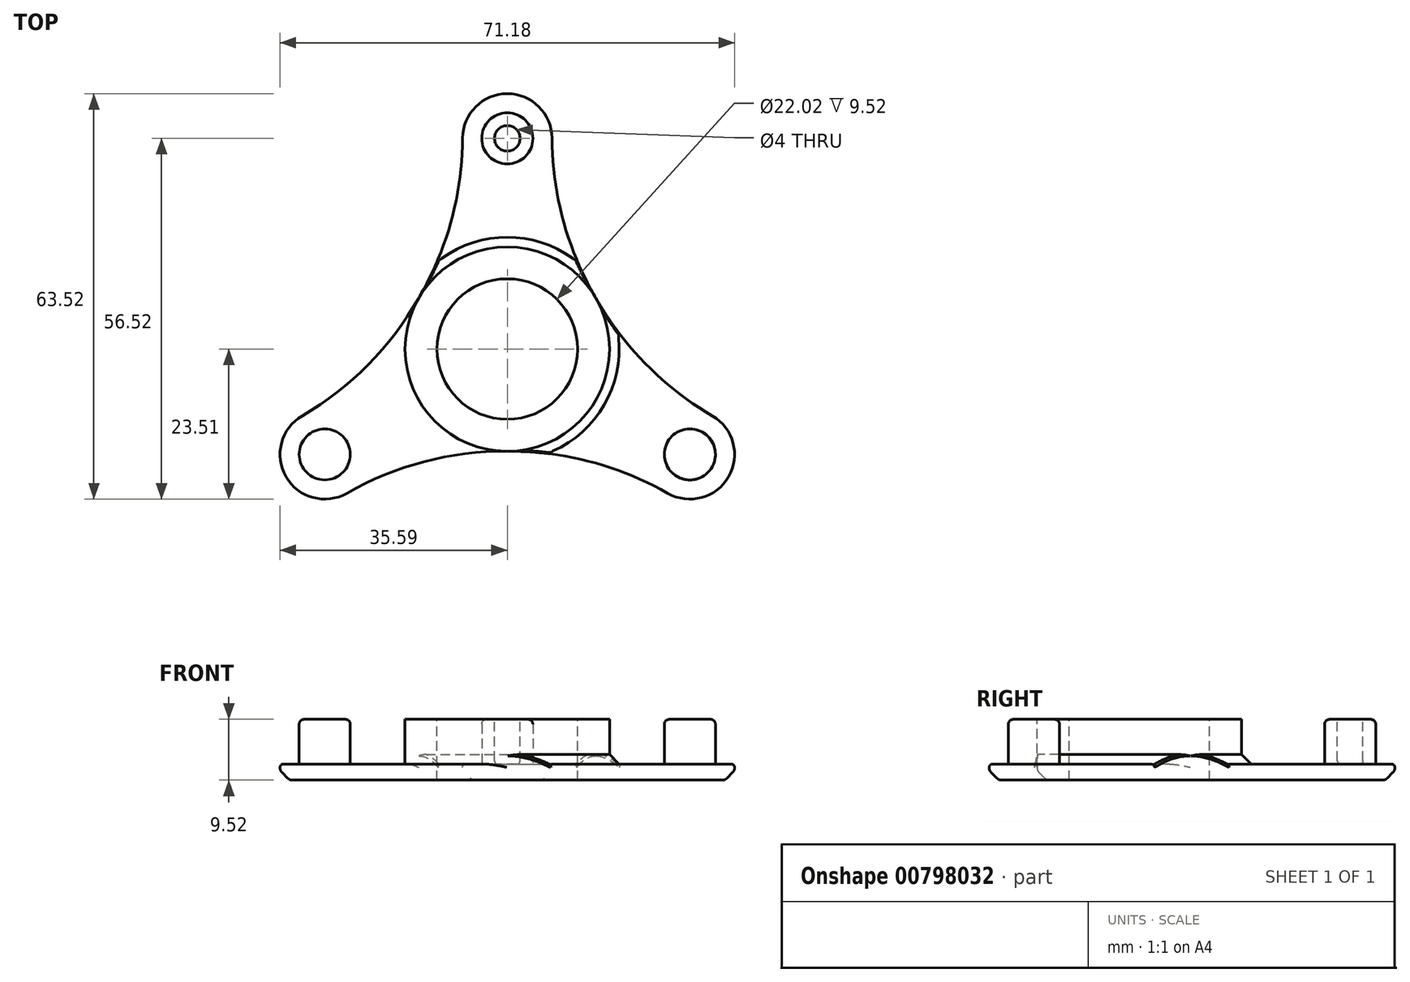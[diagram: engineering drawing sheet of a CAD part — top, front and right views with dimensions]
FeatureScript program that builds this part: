
annotation { "Feature Type Name" : "Feature", "Feature Type Description" : "" }
export const myFeature = defineFeature(function(context is Context, id is Id, definition is map)
    precondition{}
    {
        {
            var Q0;
            Q0=qCreatedBy(makeId("Top.planeOp"),FACE);
            var sketch = newSketch(context, id + "F0", { "sketchPlane" : qUnion([Q0])});
            skCircle(sketch, "E0", {"center": v(0, 0) * mm, "radius": 11.01 * mm});
            skCircle(sketch, "E1", {"center": v(0, 33.01) * mm, "radius": 4 * mm});
            skCircle(sketch, "E2.0", {"center": v(0, 33.01) * mm, "radius": 12 * mm});
            skCircle(sketch, "E3.0", {"center": v(0, 0) * mm, "radius": 16 * mm});
            skSolve(sketch);
        }
        {
            var Q0;
            Q0=makeQuery(id+"F0.imprint","IMPRINT",FACE,{"disambiguationData":[TD([[makeQuery(id+"F0.imprint","IMPRINT",EDGE,{"derivedFrom":sQuery(id+"F0.wireOp",EDGE,"E0")}),-1.0]])]});
            var Q1;
            Q1=makeQuery(id+"F0.imprint","IMPRINT",FACE,{"disambiguationData":[TD([[makeQuery(id+"F0.imprint","IMPRINT",EDGE,{"derivedFrom":sQuery(id+"F0.wireOp",EDGE,"E1")}),1.0]])]});
            extrude(context, id + "F1", {"entities" : qUnion([Q0, Q1]), "depth" : 7.02 * mm, "offsetDistance" : 25 * mm});
        }
        {
            var Q0;
            Q0=makeQuery(id+"F1.opExtrude","CAP_FACE",FACE,{"disambiguationData":[OSD([sQuery(id+"F0.wireOp",EDGE,"E0"),sQuery(id+"F0.wireOp",EDGE,"E3.0")])],"isStart":true});
            var sketch = newSketch(context, id + "F2", { "sketchPlane" : qUnion([Q0])});
            skCircle(sketch, "E4", {"center": v(-57, -33.3) * mm, "radius": 50 * mm});
            skCircle(sketch, "E5", {"center": v(57, -33.3) * mm, "radius": 50 * mm});
            skCircle(sketch, "E6", {"center": v(0, -33.01) * mm, "radius": 7 * mm});
            skSolve(sketch);
        }
        {
            var Q0;
            {var subQ0=sQuery(id+"F2.wireOp",EDGE,"E6");var subQ1=makeQuery(id+"F2.imprint","INTERSECT",VERTEX,{"derivedFrom":[sQuery(id+"F2.wireOp",EDGE,"E4"),subQ0]});Q0=makeQuery(id+"F2.imprint","IMPRINT",FACE,{"disambiguationData":[TD([[makeQuery(id+"F2.imprint","IMPRINT",EDGE,{"disambiguationData":[TD([[subQ1,1.0]])],"derivedFrom":subQ0}),1.0]])]});}
            var Q1;
            {var subQ0=sQuery(id+"F2.wireOp",EDGE,"E6");var subQ1=sQuery(id+"F2.wireOp",EDGE,"E4");var subQ2=makeQuery(id+"F2.imprint","INTERSECT",VERTEX,{"derivedFrom":[subQ1,subQ0]});Q1=makeQuery(id+"F2.imprint","IMPRINT",FACE,{"disambiguationData":[TD([[makeQuery(id+"F2.imprint","IMPRINT",EDGE,{"disambiguationData":[TD([[subQ2,-1.0]])],"derivedFrom":subQ1}),-1.0]])]});}
            var Q2;
            Q2=makeQuery(id+"F0.imprint","IMPRINT",FACE,{"disambiguationData":[TD([[makeQuery(id+"F0.imprint","IMPRINT",EDGE,{"derivedFrom":sQuery(id+"F0.wireOp",EDGE,"E0")}),-1.0]])]});
            extrude(context, id + "F3", {"entities" : qUnion([Q0, Q1, Q2]), "depth" : 2.5 * mm, "offsetDistance" : 25 * mm});
        }
        {
            var Q0;
            Q0=makeQuery(id+"F3.opExtrude","SWEPT_BODY",BODY,{"disambiguationData":[OSD([sQuery(id+"F0.wireOp",EDGE,"E3.0"),sQuery(id+"F2.wireOp",EDGE,"E4"),sQuery(id+"F2.wireOp",EDGE,"E5"),sQuery(id+"F2.wireOp",EDGE,"E6")])]});
            var Q1;
            Q1=makeQuery(id+"F1.opExtrude","SWEPT_BODY",BODY,{"disambiguationData":[OSD([sQuery(id+"F0.wireOp",EDGE,"E1")])]});
            var Q2;
            Q2=makeQuery(id+"F1.opExtrude","CAP_EDGE",EDGE,{"disambiguationData":[OSD([sQuery(id+"F0.wireOp",EDGE,"E0")])],"isStart":false});
            circularPattern(context, id + "F4", {"entities" : qUnion([Q0, Q1]), "axis" : qUnion([Q2]), "angle" : 360 * degree, "instanceCount" : 3, "equalSpace" : true});
        }
        {
            var Q0;
            Q0=makeQuery(id+"F4.opPattern","COPY",BODY,{"derivedFrom":makeQuery(id+"F3.opExtrude","SWEPT_BODY",BODY,{"disambiguationData":[OSD([sQuery(id+"F0.wireOp",EDGE,"E3.0"),sQuery(id+"F2.wireOp",EDGE,"E4"),sQuery(id+"F2.wireOp",EDGE,"E5"),sQuery(id+"F2.wireOp",EDGE,"E6")])]}),"instanceName":"2"});
            var Q1;
            Q1=makeQuery(id+"F4.opPattern","COPY",BODY,{"derivedFrom":makeQuery(id+"F1.opExtrude","SWEPT_BODY",BODY,{"disambiguationData":[OSD([sQuery(id+"F0.wireOp",EDGE,"E1")])]}),"instanceName":"2"});
            var Q2;
            Q2=makeQuery(id+"F4.opPattern","COPY",BODY,{"derivedFrom":makeQuery(id+"F3.opExtrude","SWEPT_BODY",BODY,{"disambiguationData":[OSD([sQuery(id+"F0.wireOp",EDGE,"E3.0"),sQuery(id+"F2.wireOp",EDGE,"E4"),sQuery(id+"F2.wireOp",EDGE,"E5"),sQuery(id+"F2.wireOp",EDGE,"E6")])]}),"instanceName":"1"});
            var Q3;
            Q3=makeQuery(id+"F3.opExtrude","SWEPT_BODY",BODY,{"disambiguationData":[OSD([sQuery(id+"F0.wireOp",EDGE,"E3.0"),sQuery(id+"F2.wireOp",EDGE,"E4"),sQuery(id+"F2.wireOp",EDGE,"E5"),sQuery(id+"F2.wireOp",EDGE,"E6")])]});
            var Q4;
            Q4=makeQuery(id+"F4.opPattern","COPY",BODY,{"derivedFrom":makeQuery(id+"F1.opExtrude","SWEPT_BODY",BODY,{"disambiguationData":[OSD([sQuery(id+"F0.wireOp",EDGE,"E1")])]}),"instanceName":"1"});
            var Q5;
            Q5=makeQuery(id+"F3.opExtrude","SWEPT_BODY",BODY,{"disambiguationData":[OSD([sQuery(id+"F0.wireOp",EDGE,"E0"),sQuery(id+"F0.wireOp",EDGE,"E3.0")])]});
            var Q6;
            Q6=makeQuery(id+"F1.opExtrude","SWEPT_BODY",BODY,{"disambiguationData":[OSD([sQuery(id+"F0.wireOp",EDGE,"E1")])]});
            var Q7;
            Q7=makeQuery(id+"F1.opExtrude","SWEPT_BODY",BODY,{"disambiguationData":[OSD([sQuery(id+"F0.wireOp",EDGE,"E0"),sQuery(id+"F0.wireOp",EDGE,"E3.0")])]});
            booleanBodies(context, id + "F5", {"operationType" : BooleanOperationType.UNION, "tools" : qUnion([Q0, Q1, Q2, Q3, Q4, Q5, Q6, Q7])});
        }
        {
            var Q0;
            Q0=makeQuery(id+"F4.opPattern","COPY",EDGE,{"derivedFrom":makeQuery(id+"F3.opExtrude","CAP_EDGE",EDGE,{"disambiguationData":[OSD([sQuery(id+"F2.wireOp",EDGE,"E4")])],"isStart":false}),"instanceName":"2"});
            var Q1;
            {var subQ0=sQuery(id+"F0.wireOp",EDGE,"E3.0");var subQ1=makeQuery(id+"F1.opExtrude","CAP_EDGE",EDGE,{"disambiguationData":[OSD([subQ0])],"isStart":true});Q1=makeQuery(id+"F4.opPattern","COPY",EDGE,{"derivedFrom":makeQuery(id+"F3.opExtrude","CAP_EDGE",EDGE,{"disambiguationData":[OSD([subQ0]),TDD([makeQuery(id+"F2.imprint","IMPRINT",EDGE,{"disambiguationData":[TD([[makeQuery(id+"F2.imprint","INTERSECT",VERTEX,{"derivedFrom":[subQ1,sQuery(id+"F2.wireOp",EDGE,"E4")]}),1.0]])],"derivedFrom":subQ1})])],"isStart":true}),"instanceName":"2"});}
            var Q2;
            {var subQ0=sQuery(id+"F0.wireOp",EDGE,"E3.0");var subQ1=makeQuery(id+"F1.opExtrude","CAP_EDGE",EDGE,{"disambiguationData":[OSD([subQ0])],"isStart":true});Q2=makeQuery(id+"F4.opPattern","COPY",EDGE,{"derivedFrom":makeQuery(id+"F3.opExtrude","CAP_EDGE",EDGE,{"disambiguationData":[OSD([subQ0]),TDD([makeQuery(id+"F2.imprint","IMPRINT",EDGE,{"disambiguationData":[TD([[makeQuery(id+"F2.imprint","INTERSECT",VERTEX,{"derivedFrom":[subQ1,sQuery(id+"F2.wireOp",EDGE,"E4")]}),1.0]])],"derivedFrom":subQ1})])],"isStart":true}),"instanceName":"1"});}
            var Q3;
            {var subQ0=sQuery(id+"F0.wireOp",EDGE,"E3.0");var subQ1=makeQuery(id+"F1.opExtrude","CAP_EDGE",EDGE,{"disambiguationData":[OSD([subQ0])],"isStart":true});Q3=makeQuery(id+"F3.opExtrude","CAP_EDGE",EDGE,{"disambiguationData":[OSD([subQ0]),TDD([makeQuery(id+"F2.imprint","IMPRINT",EDGE,{"disambiguationData":[TD([[makeQuery(id+"F2.imprint","INTERSECT",VERTEX,{"derivedFrom":[subQ1,sQuery(id+"F2.wireOp",EDGE,"E4")]}),1.0]])],"derivedFrom":subQ1})])],"isStart":true});}
            chamfer(context, id + "F6", {"entities" : qUnion([Q0, Q1, Q2, Q3]), "width" : 1.5 * mm, "tangentPropagation" : true});
        }
        {
            var Q0;
            Q0=makeQuery(id+"F1.opExtrude","CAP_FACE",FACE,{"disambiguationData":[OSD([sQuery(id+"F0.wireOp",EDGE,"E1")])],"isStart":false});
            var sketch = newSketch(context, id + "F7", { "sketchPlane" : qUnion([Q0])});
            skCircle(sketch, "E7", {"center": v(0, 33.01) * mm, "radius": 2 * mm});
            skSolve(sketch);
        }
        {
            var Q0;
            Q0 = qSketchRegion(id + "F7", true);
            extrude(context, id + "F8", {"entities" : qUnion([Q0]), "operationType" : NewBodyOperationType.REMOVE, "oppositeDirection" : true, "depth" : 7 * mm, "offsetDistance" : 25 * mm});
        }
        {
            var Q0;
            Q0=makeQuery(id+"F1.opExtrude","CAP_EDGE",EDGE,{"disambiguationData":[OSD([sQuery(id+"F0.wireOp",EDGE,"E1")])],"isStart":false});
            var Q1;
            Q1=makeQuery(id+"F4.opPattern","COPY",EDGE,{"derivedFrom":makeQuery(id+"F1.opExtrude","CAP_EDGE",EDGE,{"disambiguationData":[OSD([sQuery(id+"F0.wireOp",EDGE,"E1")])],"isStart":false}),"instanceName":"2"});
            var Q2;
            Q2=makeQuery(id+"F4.opPattern","COPY",EDGE,{"derivedFrom":makeQuery(id+"F1.opExtrude","CAP_EDGE",EDGE,{"disambiguationData":[OSD([sQuery(id+"F0.wireOp",EDGE,"E1")])],"isStart":false}),"instanceName":"1"});
            var Q3;
            Q3=makeQuery(id+"F8.boolean.opBoolean","COPY",EDGE,{"derivedFrom":makeQuery(id+"F8.opExtrude","CAP_EDGE",EDGE,{"disambiguationData":[OSD([sQuery(id+"F7.wireOp",EDGE,"E7")])],"isStart":true})});
            var Q4;
            Q4=makeQuery(id+"FUZLd3Gfhil9h8j_8.2.F8.boolean.opBoolean","COPY",EDGE,{"derivedFrom":makeQuery(id+"FUZLd3Gfhil9h8j_8.2.F8.opExtrude","CAP_EDGE",EDGE,{"disambiguationData":[OSD([sQuery(id+"FUZLd3Gfhil9h8j_8.2.F7.wireOp",EDGE,"E7")])],"isStart":true})});
            var Q5;
            Q5=makeQuery(id+"FUZLd3Gfhil9h8j_8.1.F8.boolean.opBoolean","COPY",EDGE,{"derivedFrom":makeQuery(id+"FUZLd3Gfhil9h8j_8.1.F8.opExtrude","CAP_EDGE",EDGE,{"disambiguationData":[OSD([sQuery(id+"FUZLd3Gfhil9h8j_8.1.F7.wireOp",EDGE,"E7")])],"isStart":true})});
            fillet(context, id + "F9", {"entities" : qUnion([Q0, Q1, Q2, Q3, Q4, Q5]), "radius" : .75 * mm, "tangentPropagation" : true, "allowEdgeOverflow" : false});
        }
        {
            var Q0;
            Q0=makeQuery(id+"F8.boolean.opBoolean","COPY",FACE,{"derivedFrom":makeQuery(id+"F8.opExtrude","CAP_FACE",FACE,{"disambiguationData":[OSD([sQuery(id+"F7.wireOp",EDGE,"E7")])],"isStart":false})});
            var Q1;
            Q1=makeQuery(id+"FUZLd3Gfhil9h8j_8.2.F8.boolean.opBoolean","COPY",FACE,{"derivedFrom":makeQuery(id+"FUZLd3Gfhil9h8j_8.2.F8.opExtrude","CAP_FACE",FACE,{"disambiguationData":[OSD([sQuery(id+"FUZLd3Gfhil9h8j_8.2.F7.wireOp",EDGE,"E7")])],"isStart":false})});
            var Q2;
            Q2=makeQuery(id+"FUZLd3Gfhil9h8j_8.1.F8.boolean.opBoolean","COPY",FACE,{"derivedFrom":makeQuery(id+"FUZLd3Gfhil9h8j_8.1.F8.opExtrude","CAP_FACE",FACE,{"disambiguationData":[OSD([sQuery(id+"FUZLd3Gfhil9h8j_8.1.F7.wireOp",EDGE,"E7")])],"isStart":false})});
            fillet(context, id + "F10", {"entities" : qUnion([Q0, Q1, Q2]), "radius" : .5 * mm, "tangentPropagation" : true, "allowEdgeOverflow" : false});
        }
        {
            var Q0;
            Q0=makeQuery(id+"F4.opPattern","COPY",EDGE,{"derivedFrom":makeQuery(id+"F3.opExtrude","CAP_EDGE",EDGE,{"disambiguationData":[OSD([sQuery(id+"F2.wireOp",EDGE,"E4")])],"isStart":true}),"instanceName":"1"});
            var Q1;
            Q1=makeQuery(id+"F4.opPattern","COPY",EDGE,{"derivedFrom":makeQuery(id+"F3.opExtrude","CAP_EDGE",EDGE,{"disambiguationData":[OSD([sQuery(id+"F2.wireOp",EDGE,"E5")])],"isStart":true}),"instanceName":"2"});
            var Q2;
            Q2=makeQuery(id+"F3.opExtrude","CAP_EDGE",EDGE,{"disambiguationData":[OSD([sQuery(id+"F2.wireOp",EDGE,"E5")])],"isStart":true});
            var Q3;
            {var subQ0=sQuery(id+"F2.wireOp",EDGE,"E4");var subQ1=sQuery(id+"F0.wireOp",EDGE,"E3.0");var subQ2=makeQuery(id+"F1.opExtrude","CAP_EDGE",EDGE,{"disambiguationData":[OSD([subQ1])],"isStart":true});Q3=makeQuery(id+"F6.opChamfer","BLEND_EDGE",EDGE,{"blendedFrom":[makeQuery(id+"F3.opExtrude","CAP_EDGE",EDGE,{"disambiguationData":[OSD([subQ1]),TDD([makeQuery(id+"F2.imprint","IMPRINT",EDGE,{"disambiguationData":[TD([[makeQuery(id+"F2.imprint","INTERSECT",VERTEX,{"derivedFrom":[subQ2,subQ0]}),1.0]])],"derivedFrom":subQ2})])],"isStart":true}),makeQuery(id+"F3.opExtrude","SWEPT_FACE",FACE,{"disambiguationData":[OSD([subQ0])]})],"blendedInto":[makeQuery(id+"F3.opExtrude","SWEPT_FACE",FACE,{"disambiguationData":[OSD([subQ0])]})]});}
            var Q4;
            {var subQ0=sQuery(id+"F2.wireOp",EDGE,"E5");var subQ1=sQuery(id+"F0.wireOp",EDGE,"E3.0");var subQ2=makeQuery(id+"F1.opExtrude","CAP_EDGE",EDGE,{"disambiguationData":[OSD([subQ1])],"isStart":true});Q4=makeQuery(id+"F6.opChamfer","BLEND_EDGE",EDGE,{"blendedFrom":[makeQuery(id+"F4.opPattern","COPY",EDGE,{"derivedFrom":makeQuery(id+"F3.opExtrude","CAP_EDGE",EDGE,{"disambiguationData":[OSD([subQ1]),TDD([makeQuery(id+"F2.imprint","IMPRINT",EDGE,{"disambiguationData":[TD([[makeQuery(id+"F2.imprint","INTERSECT",VERTEX,{"derivedFrom":[subQ2,sQuery(id+"F2.wireOp",EDGE,"E4")]}),1.0]])],"derivedFrom":subQ2})])],"isStart":true}),"instanceName":"1"}),makeQuery(id+"F4.opPattern","COPY",FACE,{"derivedFrom":makeQuery(id+"F3.opExtrude","SWEPT_FACE",FACE,{"disambiguationData":[OSD([subQ0])]}),"instanceName":"1"})],"blendedInto":[makeQuery(id+"F4.opPattern","COPY",FACE,{"derivedFrom":makeQuery(id+"F3.opExtrude","SWEPT_FACE",FACE,{"disambiguationData":[OSD([subQ0])]}),"instanceName":"1"})]});}
            var Q5;
            {var subQ0=sQuery(id+"F2.wireOp",EDGE,"E5");var subQ1=sQuery(id+"F0.wireOp",EDGE,"E3.0");var subQ2=makeQuery(id+"F1.opExtrude","CAP_EDGE",EDGE,{"disambiguationData":[OSD([subQ1])],"isStart":true});Q5=makeQuery(id+"F6.opChamfer","BLEND_EDGE",EDGE,{"blendedFrom":[makeQuery(id+"F3.opExtrude","CAP_EDGE",EDGE,{"disambiguationData":[OSD([subQ1]),TDD([makeQuery(id+"F2.imprint","IMPRINT",EDGE,{"disambiguationData":[TD([[makeQuery(id+"F2.imprint","INTERSECT",VERTEX,{"derivedFrom":[subQ2,sQuery(id+"F2.wireOp",EDGE,"E4")]}),1.0]])],"derivedFrom":subQ2})])],"isStart":true}),makeQuery(id+"F3.opExtrude","SWEPT_FACE",FACE,{"disambiguationData":[OSD([subQ0])]})],"blendedInto":[makeQuery(id+"F3.opExtrude","SWEPT_FACE",FACE,{"disambiguationData":[OSD([subQ0])]})]});}
            var Q6;
            {var subQ0=sQuery(id+"F2.wireOp",EDGE,"E4");var subQ1=sQuery(id+"F0.wireOp",EDGE,"E3.0");var subQ2=makeQuery(id+"F1.opExtrude","CAP_EDGE",EDGE,{"disambiguationData":[OSD([subQ1])],"isStart":true});Q6=makeQuery(id+"F6.opChamfer","BLEND_EDGE",EDGE,{"blendedFrom":[makeQuery(id+"F4.opPattern","COPY",EDGE,{"derivedFrom":makeQuery(id+"F3.opExtrude","CAP_EDGE",EDGE,{"disambiguationData":[OSD([subQ1]),TDD([makeQuery(id+"F2.imprint","IMPRINT",EDGE,{"disambiguationData":[TD([[makeQuery(id+"F2.imprint","INTERSECT",VERTEX,{"derivedFrom":[subQ2,subQ0]}),1.0]])],"derivedFrom":subQ2})])],"isStart":true}),"instanceName":"2"}),makeQuery(id+"F4.opPattern","COPY",FACE,{"derivedFrom":makeQuery(id+"F3.opExtrude","SWEPT_FACE",FACE,{"disambiguationData":[OSD([subQ0])]}),"instanceName":"2"})],"blendedInto":[makeQuery(id+"F4.opPattern","COPY",FACE,{"derivedFrom":makeQuery(id+"F3.opExtrude","SWEPT_FACE",FACE,{"disambiguationData":[OSD([subQ0])]}),"instanceName":"2"})]});}
            var Q7;
            {var subQ0=sQuery(id+"F2.wireOp",EDGE,"E4");var subQ1=sQuery(id+"F0.wireOp",EDGE,"E3.0");var subQ2=makeQuery(id+"F1.opExtrude","CAP_EDGE",EDGE,{"disambiguationData":[OSD([subQ1])],"isStart":true});Q7=makeQuery(id+"F6.opChamfer","BLEND_EDGE",EDGE,{"blendedFrom":[makeQuery(id+"F4.opPattern","COPY",EDGE,{"derivedFrom":makeQuery(id+"F3.opExtrude","CAP_EDGE",EDGE,{"disambiguationData":[OSD([subQ1]),TDD([makeQuery(id+"F2.imprint","IMPRINT",EDGE,{"disambiguationData":[TD([[makeQuery(id+"F2.imprint","INTERSECT",VERTEX,{"derivedFrom":[subQ2,subQ0]}),1.0]])],"derivedFrom":subQ2})])],"isStart":true}),"instanceName":"1"}),makeQuery(id+"F4.opPattern","COPY",FACE,{"derivedFrom":makeQuery(id+"F3.opExtrude","SWEPT_FACE",FACE,{"disambiguationData":[OSD([subQ0])]}),"instanceName":"1"})],"blendedInto":[makeQuery(id+"F4.opPattern","COPY",FACE,{"derivedFrom":makeQuery(id+"F3.opExtrude","SWEPT_FACE",FACE,{"disambiguationData":[OSD([subQ0])]}),"instanceName":"1"})]});}
            var Q8;
            {var subQ0=sQuery(id+"F2.wireOp",EDGE,"E5");var subQ1=sQuery(id+"F0.wireOp",EDGE,"E3.0");var subQ2=makeQuery(id+"F1.opExtrude","CAP_EDGE",EDGE,{"disambiguationData":[OSD([subQ1])],"isStart":true});Q8=makeQuery(id+"F6.opChamfer","BLEND_EDGE",EDGE,{"blendedFrom":[makeQuery(id+"F4.opPattern","COPY",EDGE,{"derivedFrom":makeQuery(id+"F3.opExtrude","CAP_EDGE",EDGE,{"disambiguationData":[OSD([subQ1]),TDD([makeQuery(id+"F2.imprint","IMPRINT",EDGE,{"disambiguationData":[TD([[makeQuery(id+"F2.imprint","INTERSECT",VERTEX,{"derivedFrom":[subQ2,sQuery(id+"F2.wireOp",EDGE,"E4")]}),1.0]])],"derivedFrom":subQ2})])],"isStart":true}),"instanceName":"2"}),makeQuery(id+"F4.opPattern","COPY",FACE,{"derivedFrom":makeQuery(id+"F3.opExtrude","SWEPT_FACE",FACE,{"disambiguationData":[OSD([subQ0])]}),"instanceName":"2"})],"blendedInto":[makeQuery(id+"F4.opPattern","COPY",FACE,{"derivedFrom":makeQuery(id+"F3.opExtrude","SWEPT_FACE",FACE,{"disambiguationData":[OSD([subQ0])]}),"instanceName":"2"})]});}
            fillet(context, id + "F11", {"entities" : qUnion([Q0, Q1, Q2, Q3, Q4, Q5, Q6, Q7, Q8]), "radius" : .5 * mm, "tangentPropagation" : true, "allowEdgeOverflow" : false});
        }
        {
            var Q0;
            {var subQ0=sQuery(id+"F2.wireOp",EDGE,"E5");var subQ1=sQuery(id+"F0.wireOp",EDGE,"E3.0");var subQ2=makeQuery(id+"F3.opExtrude","CAP_FACE",FACE,{"disambiguationData":[OSD([subQ1,sQuery(id+"F2.wireOp",EDGE,"E4"),subQ0,sQuery(id+"F2.wireOp",EDGE,"E6")])],"isStart":false});Q0=makeQuery(id+"F6.opChamfer","BLEND_EDGE",EDGE,{"blendedFrom":[makeQuery(id+"F4.opPattern","COPY",EDGE,{"derivedFrom":makeQuery(id+"F3.opExtrude","CAP_EDGE",EDGE,{"disambiguationData":[OSD([subQ0])],"isStart":false}),"instanceName":"2"}),makeQuery(id+"F5.opBoolean","MERGE",FACE,{"derivedFrom":[makeQuery(id+"F3.opExtrude","CAP_FACE",FACE,{"disambiguationData":[OSD([sQuery(id+"F0.wireOp",EDGE,"E0"),subQ1])],"isStart":false}),subQ2,makeQuery(id+"F4.opPattern","COPY",FACE,{"derivedFrom":subQ2,"instanceName":"1"}),makeQuery(id+"F4.opPattern","COPY",FACE,{"derivedFrom":subQ2,"instanceName":"2"})]})],"blendedInto":[makeQuery(id+"F5.opBoolean","MERGE",FACE,{"derivedFrom":[makeQuery(id+"F3.opExtrude","CAP_FACE",FACE,{"disambiguationData":[OSD([sQuery(id+"F0.wireOp",EDGE,"E0"),subQ1])],"isStart":false}),subQ2,makeQuery(id+"F4.opPattern","COPY",FACE,{"derivedFrom":subQ2,"instanceName":"1"}),makeQuery(id+"F4.opPattern","COPY",FACE,{"derivedFrom":subQ2,"instanceName":"2"})]})]});}
            var Q1;
            {var subQ0=sQuery(id+"F2.wireOp",EDGE,"E6");var subQ1=sQuery(id+"F0.wireOp",EDGE,"E3.0");var subQ2=makeQuery(id+"F3.opExtrude","CAP_FACE",FACE,{"disambiguationData":[OSD([subQ1,sQuery(id+"F2.wireOp",EDGE,"E4"),sQuery(id+"F2.wireOp",EDGE,"E5"),subQ0])],"isStart":false});Q1=makeQuery(id+"F6.opChamfer","BLEND_EDGE",EDGE,{"blendedFrom":[makeQuery(id+"F4.opPattern","COPY",EDGE,{"derivedFrom":makeQuery(id+"F3.opExtrude","CAP_EDGE",EDGE,{"disambiguationData":[OSD([subQ0])],"isStart":false}),"instanceName":"2"}),makeQuery(id+"F5.opBoolean","MERGE",FACE,{"derivedFrom":[makeQuery(id+"F3.opExtrude","CAP_FACE",FACE,{"disambiguationData":[OSD([sQuery(id+"F0.wireOp",EDGE,"E0"),subQ1])],"isStart":false}),subQ2,makeQuery(id+"F4.opPattern","COPY",FACE,{"derivedFrom":subQ2,"instanceName":"1"}),makeQuery(id+"F4.opPattern","COPY",FACE,{"derivedFrom":subQ2,"instanceName":"2"})]})],"blendedInto":[makeQuery(id+"F5.opBoolean","MERGE",FACE,{"derivedFrom":[makeQuery(id+"F3.opExtrude","CAP_FACE",FACE,{"disambiguationData":[OSD([sQuery(id+"F0.wireOp",EDGE,"E0"),subQ1])],"isStart":false}),subQ2,makeQuery(id+"F4.opPattern","COPY",FACE,{"derivedFrom":subQ2,"instanceName":"1"}),makeQuery(id+"F4.opPattern","COPY",FACE,{"derivedFrom":subQ2,"instanceName":"2"})]})]});}
            var Q2;
            {var subQ0=sQuery(id+"F2.wireOp",EDGE,"E4");var subQ1=sQuery(id+"F0.wireOp",EDGE,"E3.0");var subQ2=makeQuery(id+"F3.opExtrude","CAP_FACE",FACE,{"disambiguationData":[OSD([subQ1,subQ0,sQuery(id+"F2.wireOp",EDGE,"E5"),sQuery(id+"F2.wireOp",EDGE,"E6")])],"isStart":false});Q2=makeQuery(id+"F6.opChamfer","BLEND_EDGE",EDGE,{"blendedFrom":[makeQuery(id+"F3.opExtrude","CAP_EDGE",EDGE,{"disambiguationData":[OSD([subQ0])],"isStart":false}),makeQuery(id+"F5.opBoolean","MERGE",FACE,{"derivedFrom":[makeQuery(id+"F3.opExtrude","CAP_FACE",FACE,{"disambiguationData":[OSD([sQuery(id+"F0.wireOp",EDGE,"E0"),subQ1])],"isStart":false}),subQ2,makeQuery(id+"F4.opPattern","COPY",FACE,{"derivedFrom":subQ2,"instanceName":"1"}),makeQuery(id+"F4.opPattern","COPY",FACE,{"derivedFrom":subQ2,"instanceName":"2"})]})],"blendedInto":[makeQuery(id+"F5.opBoolean","MERGE",FACE,{"derivedFrom":[makeQuery(id+"F3.opExtrude","CAP_FACE",FACE,{"disambiguationData":[OSD([sQuery(id+"F0.wireOp",EDGE,"E0"),subQ1])],"isStart":false}),subQ2,makeQuery(id+"F4.opPattern","COPY",FACE,{"derivedFrom":subQ2,"instanceName":"1"}),makeQuery(id+"F4.opPattern","COPY",FACE,{"derivedFrom":subQ2,"instanceName":"2"})]})]});}
            var Q3;
            {var subQ0=sQuery(id+"F2.wireOp",EDGE,"E4");Q3=makeQuery(id+"F6.opChamfer","BLEND_EDGE",EDGE,{"blendedFrom":[makeQuery(id+"F4.opPattern","COPY",EDGE,{"derivedFrom":makeQuery(id+"F3.opExtrude","CAP_EDGE",EDGE,{"disambiguationData":[OSD([subQ0])],"isStart":false}),"instanceName":"1"}),makeQuery(id+"F4.opPattern","COPY",FACE,{"derivedFrom":makeQuery(id+"F3.opExtrude","SWEPT_FACE",FACE,{"disambiguationData":[OSD([subQ0])]}),"instanceName":"1"})],"blendedInto":[makeQuery(id+"F4.opPattern","COPY",FACE,{"derivedFrom":makeQuery(id+"F3.opExtrude","SWEPT_FACE",FACE,{"disambiguationData":[OSD([subQ0])]}),"instanceName":"1"})]});}
            var Q4;
            {var subQ0=sQuery(id+"F2.wireOp",EDGE,"E6");Q4=makeQuery(id+"F6.opChamfer","BLEND_EDGE",EDGE,{"blendedFrom":[makeQuery(id+"F4.opPattern","COPY",EDGE,{"derivedFrom":makeQuery(id+"F3.opExtrude","CAP_EDGE",EDGE,{"disambiguationData":[OSD([subQ0])],"isStart":false}),"instanceName":"2"}),makeQuery(id+"F4.opPattern","COPY",FACE,{"derivedFrom":makeQuery(id+"F3.opExtrude","SWEPT_FACE",FACE,{"disambiguationData":[OSD([subQ0])]}),"instanceName":"2"})],"blendedInto":[makeQuery(id+"F4.opPattern","COPY",FACE,{"derivedFrom":makeQuery(id+"F3.opExtrude","SWEPT_FACE",FACE,{"disambiguationData":[OSD([subQ0])]}),"instanceName":"2"})]});}
            var Q5;
            {var subQ0=sQuery(id+"F2.wireOp",EDGE,"E5");Q5=makeQuery(id+"F6.opChamfer","BLEND_EDGE",EDGE,{"blendedFrom":[makeQuery(id+"F3.opExtrude","CAP_EDGE",EDGE,{"disambiguationData":[OSD([subQ0])],"isStart":false}),makeQuery(id+"F3.opExtrude","SWEPT_FACE",FACE,{"disambiguationData":[OSD([subQ0])]})],"blendedInto":[makeQuery(id+"F3.opExtrude","SWEPT_FACE",FACE,{"disambiguationData":[OSD([subQ0])]})]});}
            var Q6;
            {var subQ0=sQuery(id+"F2.wireOp",EDGE,"E4");Q6=makeQuery(id+"F6.opChamfer","BLEND_EDGE",EDGE,{"blendedFrom":[makeQuery(id+"F3.opExtrude","CAP_EDGE",EDGE,{"disambiguationData":[OSD([subQ0])],"isStart":false}),makeQuery(id+"F3.opExtrude","SWEPT_FACE",FACE,{"disambiguationData":[OSD([subQ0])]})],"blendedInto":[makeQuery(id+"F3.opExtrude","SWEPT_FACE",FACE,{"disambiguationData":[OSD([subQ0])]})]});}
            fillet(context, id + "F12", {"entities" : qUnion([Q0, Q1, Q2, Q3, Q4, Q5, Q6]), "radius" : 1 * mm, "tangentPropagation" : true, "allowEdgeOverflow" : false});
        }
    });
